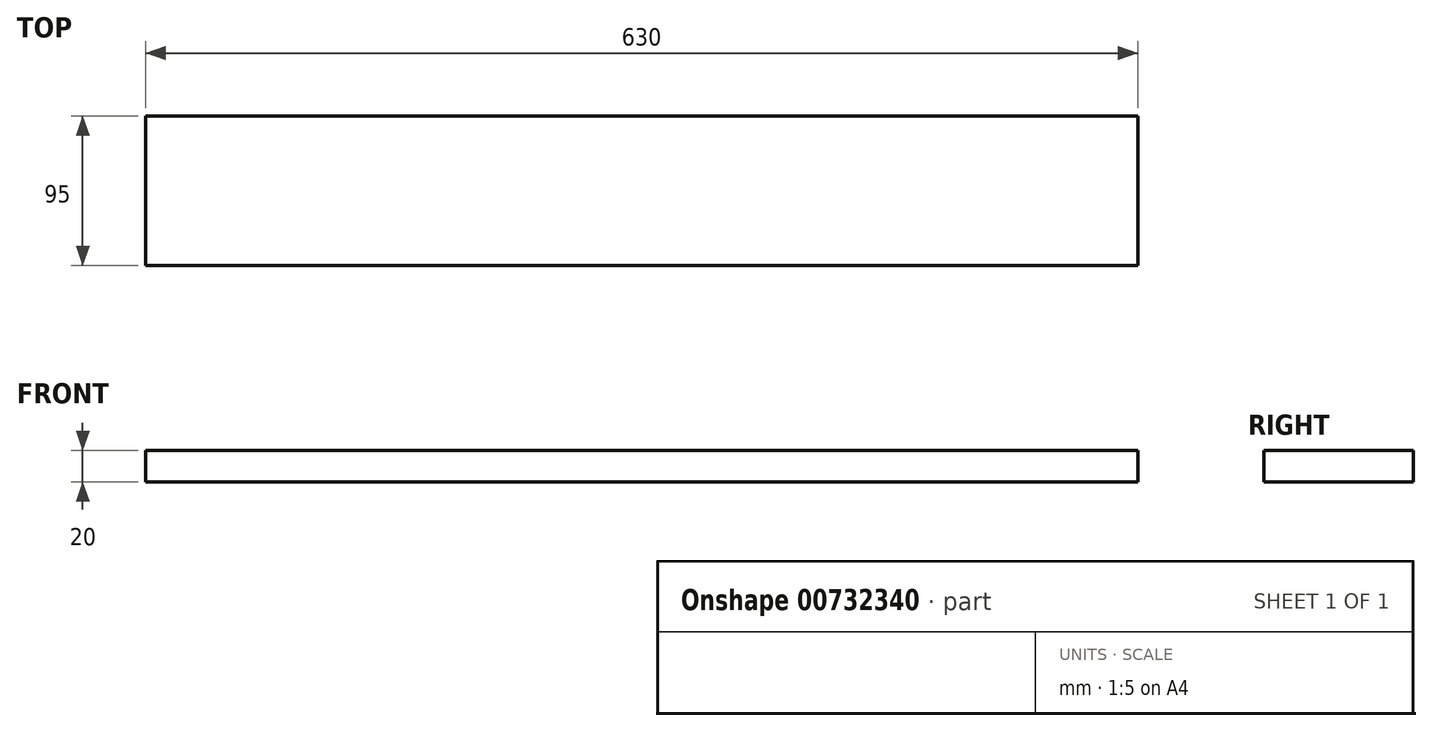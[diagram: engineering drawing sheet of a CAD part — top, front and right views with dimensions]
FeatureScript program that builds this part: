
annotation { "Feature Type Name" : "Feature", "Feature Type Description" : "" }
export const myFeature = defineFeature(function(context is Context, id is Id, definition is map)
    precondition{}
    {
        {
            var Q0;
            Q0=qCreatedBy(makeId("Top.planeOp"),FACE);
            var sketch = newSketch(context, id + "F0", { "sketchPlane" : qUnion([Q0])});
            skLineSegment(sketch, "E0.bottom", {"start": v(-315, 47.5) * mm, "end": v(315, 47.5) * mm});
            skLineSegment(sketch, "E0.top", {"start": v(-315, -47.5) * mm, "end": v(315, -47.5) * mm});
            skLineSegment(sketch, "E0.left", {"start": v(-315, 47.5) * mm, "end": v(-315, -47.5) * mm});
            skLineSegment(sketch, "E0.right", {"start": v(315, 47.5) * mm, "end": v(315, -47.5) * mm});
            skPoint(sketch, "E0.middle", {"position": v(0, 0) * mm});
            skSolve(sketch);
        }
        {
            var Q0;
            Q0=makeQuery(id+"F0.imprint","IMPRINT",FACE,{"disambiguationData":[TD([[makeQuery(id+"F0.imprint","IMPRINT",EDGE,{"derivedFrom":sQuery(id+"F0.wireOp",EDGE,"E0.bottom")}),-1.0]])]});
            extrude(context, id + "F1", {"entities" : qUnion([Q0]), "depth" : 20 * mm, "offsetDistance" : 25 * mm});
        }
    });
